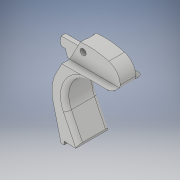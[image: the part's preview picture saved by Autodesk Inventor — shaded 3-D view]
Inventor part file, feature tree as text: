
AUTODESK INVENTOR PART (.ipt)
format: ipt  version: 2018.3 (Build 223284000, 284)  size: 265,728 bytes
history: native  units: in
note: dims shown in document units (in); Inventor stores cm internally (conversion verified against a paired STEP export)
features: extrude x5, sketch x3, plane x2, fillet x1
ambient origin geometry x8: Origin, YZ Plane, XZ Plane, XY Plane, X Axis, Y Axis, Z Axis, Center Point
bodies: Solid1 (feature_tree)
feature tree (11):
  sketch  "Sketch1"  dims[d1=0.5222in d2=0.426in]
  extrude  "Extrusion1"  Depth=0.426in
  extrude  "Extrusion2"  Depth=0.47in
  fillet  "Fillet1"  Radius=1.41in
  sketch  "Sketch3"  dims[d6=0.62in d7=0.22in d9=1.0in d10=0.75in d11=0.665in d12=0.1202in d13=1.563in d14=0.071in d15=0.124in d16=0.56in d17=0.0275in d18=0.841in d19=0.074in d20=0.428in d21=0.2096in d22=0.675in d23=0.255in d24=0.5222in d25=45.0deg d26=0.812in d27=0.73in d28=0.143in d29=0.619in d30=0.0in d32=0.309in d34=0.619in d35=0.0in d36=0.255in d37=0.0825in d38=0.75in d39=0.0in d40=4.0in d41=0.75in d42=45.0deg d43=0.527in d44=1.62in d45=0.88in d47=-0.276in d48=0.138in d49=0.0in d50=-0.149in d51=0.438in d52=0.0in d53=0.087in d54=0.0in]
  plane  "Work Plane2"
  extrude  "Extrusion3"  Depth=0.087in
  plane  "Work Plane3"
  extrude  "Extrusion4"  Depth=0.087in
  extrude  "Extrusion5"  Depth=0.75in
  sketch  "Sketch2"  dims[d3=0.115in d4=0.47in d5=1.41in]
